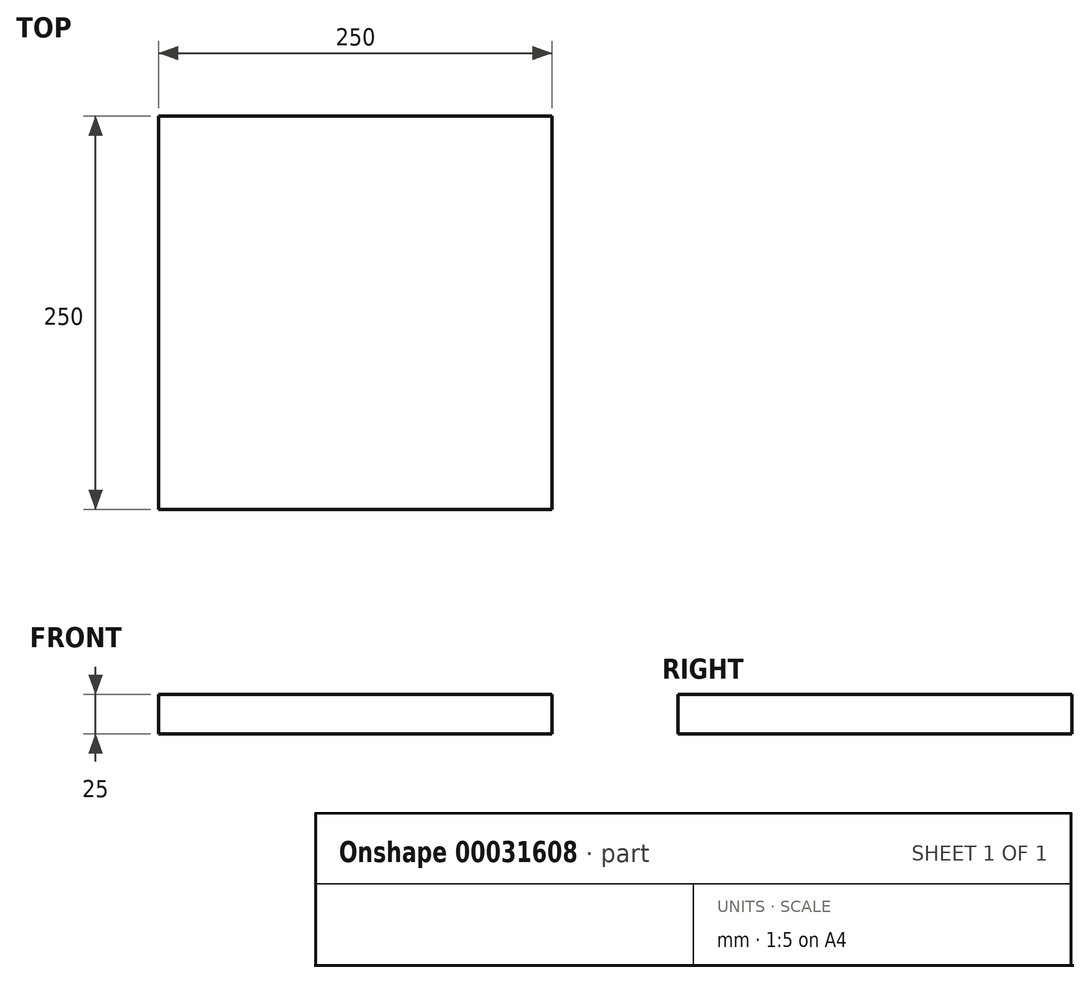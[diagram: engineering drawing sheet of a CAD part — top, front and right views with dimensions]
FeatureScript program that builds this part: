
annotation { "Feature Type Name" : "Feature", "Feature Type Description" : "" }
export const myFeature = defineFeature(function(context is Context, id is Id, definition is map)
    precondition{}
    {
        {
            var Q0;
            Q0=qCreatedBy(makeId("Top.planeOp"),FACE);
            var sketch = newSketch(context, id + "F0", { "sketchPlane" : qUnion([Q0])});
            skLineSegment(sketch, "E0", {"start": v(109.07, -468.64) * mm, "end": v(109.07, -218.64) * mm});
            skLineSegment(sketch, "E1", {"start": v(109.07, -218.64) * mm, "end": v(-140.93, -218.64) * mm});
            skLineSegment(sketch, "E2.bottom", {"start": v(109.07, -468.64) * mm, "end": v(-140.93, -468.64) * mm});
            skLineSegment(sketch, "E2.right", {"start": v(-140.93, -468.64) * mm, "end": v(-140.93, -218.64) * mm});
            skSolve(sketch);
        }
        {
            var Q0;
            Q0 = qSketchRegion(id + "F0", true);
            var Q1;
            Q1=makeQuery(id+"F0.imprint","IMPRINT",FACE,{"disambiguationData":[TD([[makeQuery(id+"F0.imprint","IMPRINT",EDGE,{"derivedFrom":sQuery(id+"F0.wireOp",EDGE,"E2.bottom")}),-1.0]])]});
            extrude(context, id + "F1", {"entities" : qUnion([Q0, Q1]), "depth" : 25 * mm});
        }
    });
